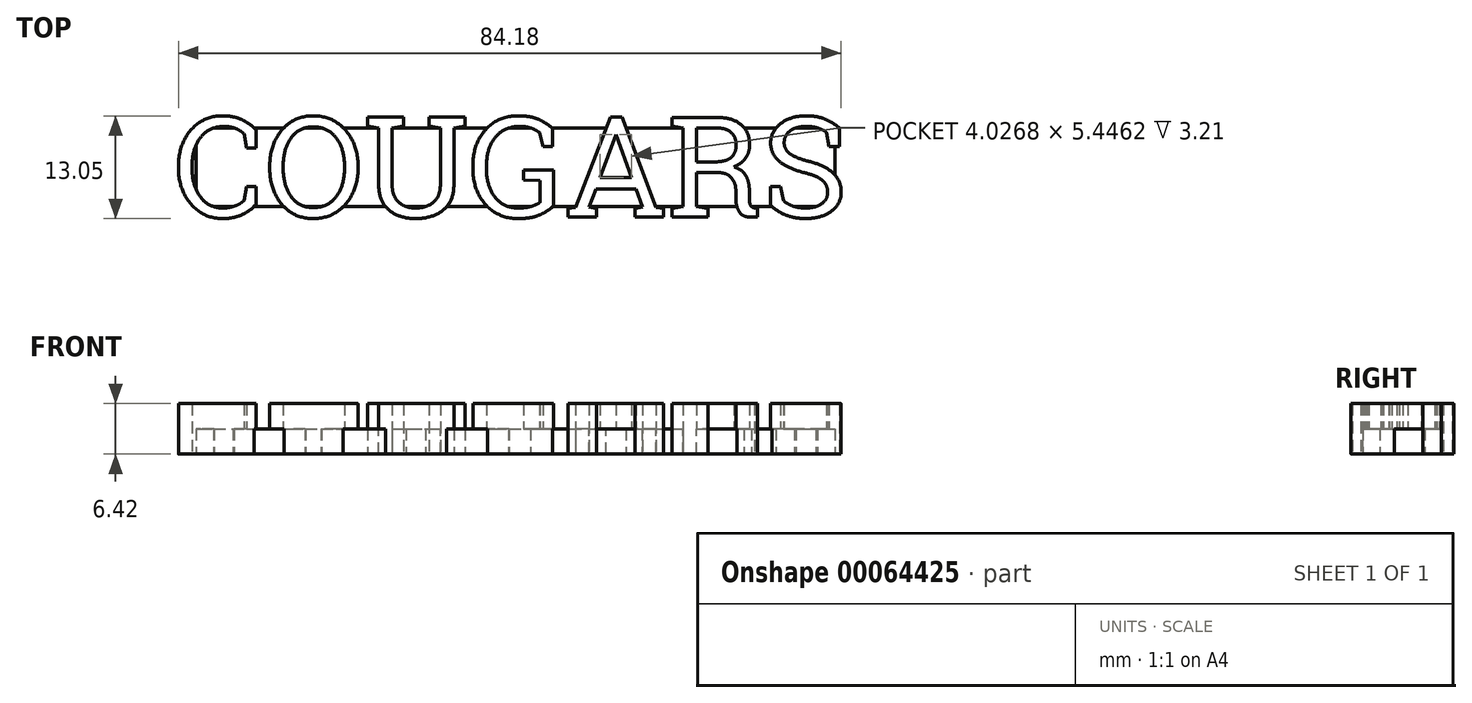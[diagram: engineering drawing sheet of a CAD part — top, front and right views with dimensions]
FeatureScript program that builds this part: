
annotation { "Feature Type Name" : "Feature", "Feature Type Description" : "" }
export const myFeature = defineFeature(function(context is Context, id is Id, definition is map)
    precondition{}
    {
        {
            var Q0;
            Q0=qCreatedBy(makeId("Top.planeOp"),FACE);
            var sketch = newSketch(context, id + "F0", { "sketchPlane" : qUnion([Q0])});
            skText(sketch, "E0", { "text": "COUGARS", "fontName": "RobotoSlab-Regular.ttf"});
            const initialGuessF0  = {"E0": [-0.07648, 0, 1, 0, 0.01285]};
            skSetInitialGuess(sketch, initialGuessF0);
            skSolve(sketch);
        }
        {
            var Q0;
            Q0 = qSketchRegion(id + "F0", true);
            extrude(context, id + "F1", {"entities" : qUnion([Q0]), "depth" : 6.42 * mm});
        }
        {
            var Q0;
            Q0=makeQuery(id+"F1.opExtrude","SWEPT_FACE",FACE,{"disambiguationData":[OSD([sQuery(id+"F0.wireOp",EDGE,"E0.sketch_text.stroke-138")])]});
            var sketch = newSketch(context, id + "F2", { "sketchPlane" : qUnion([Q0])});
            skLineSegment(sketch, "E1", {"start": v(-1.34, 3.21) * mm, "end": v(-11.33, 3.21) * mm});
            skLineSegment(sketch, "E2", {"start": v(-11.33, 3.21) * mm, "end": v(-11.33, 0) * mm});
            skLineSegment(sketch, "E3", {"start": v(-11.33, 0) * mm, "end": v(-1.34, 0) * mm});
            skLineSegment(sketch, "E4", {"start": v(-1.34, 0) * mm, "end": v(-1.34, 3.21) * mm});
            skSolve(sketch);
        }
        {
            var Q0;
            Q0 = qSketchRegion(id + "F2", true);
            extrude(context, id + "F3", {"entities" : qUnion([Q0]), "operationType" : NewBodyOperationType.ADD, "depth" : 61.86 * mm, "hasSecondDirection" : true, "secondDirectionOppositeDirection" : true, "secondDirectionDepth" : 19.3 * mm});
        }
    });
